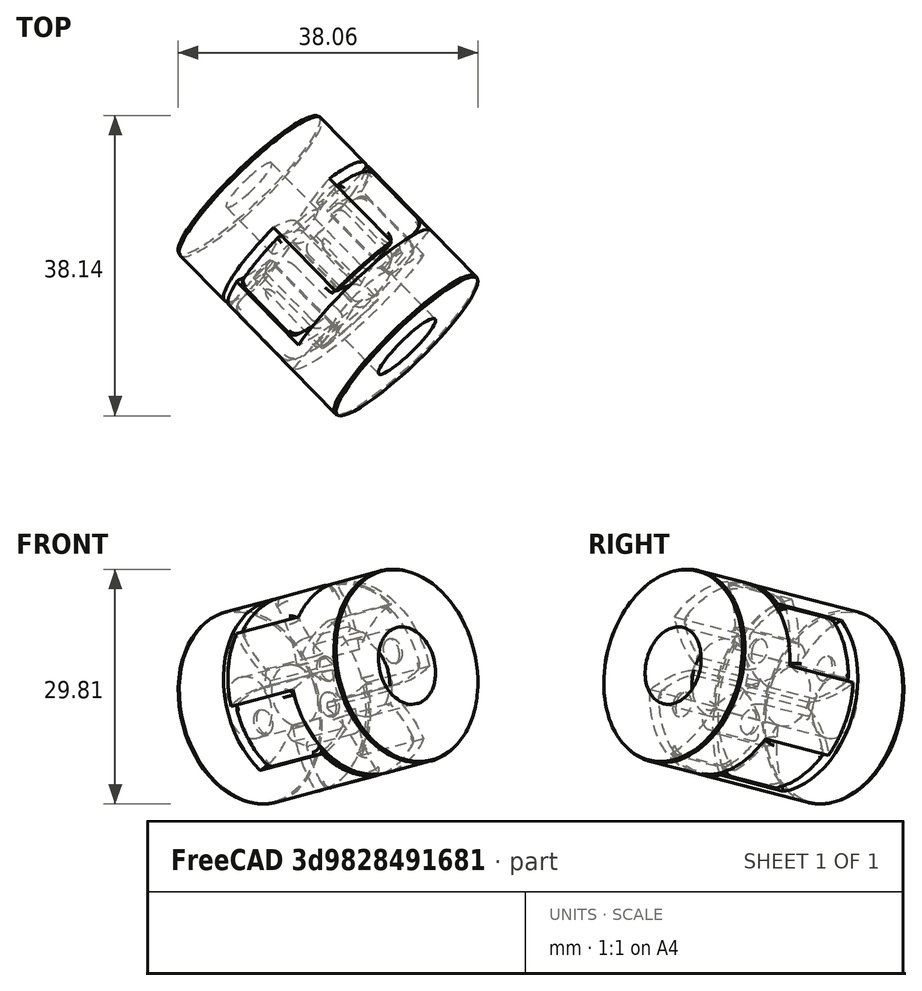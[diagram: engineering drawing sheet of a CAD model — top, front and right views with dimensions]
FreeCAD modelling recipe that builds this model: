
FCSTD DOCUMENT  (FreeCAD 0.21R38887 (Git))
Label: mufta8x10
License: All rights reserved
LicenseURL: http://en.wikipedia.org/wiki/All_rights_reserved
objects: Part::FeaturePython×5, Part::Feature×3, App::FeaturePython×2
note: 7 computed .brp shape members not serialized (recipe doc carries the construction recipe); baked Part::Feature solids carry a one-line shape summary decoded from their .brp

FEATURE [App::FeaturePython] Constraints  # WARN: FeaturePython — macro-defined, semantics opaque (R4)
  TreeRank = 9
  _LinkVersion = 1
  _Version = 1
FEATURE [Part::Feature] Solid  label="среднМуфта_8_10мм"
  InvalidShape = false
  Placement = pos=(-45.9665,58.8208,-32.3728) rot=(-0.885788,0.302008,-0.352379;2.03811rad)
  TreeRank = 1
  ValidateShape = false
  shape: bbox 24.52 x 25.47 x 27.67 mm, 100 faces (baked)
FEATURE [Part::Feature] Solid001  label="8мм^Муфта_8_10мм"
  InvalidShape = false
  Placement = pos=(-38.8086,51.5065,-30.4665) rot=(0.394242,0.904466,-0.162836;3.08092rad)
  TreeRank = 5
  ValidateShape = false
  shape: bbox 31.75 x 31.69 x 28.16 mm, 18 faces (baked)
FEATURE [Part::Feature] Solid002  label="10мм^Муфта_8_10мм"
  InvalidShape = false
  Placement = pos=(-46.2484,59.1089,-32.4479) rot=(0.798462,-0.457126,-0.391783;1.43227rad)
  TreeRank = 6
  ValidateShape = false
  shape: bbox 31.75 x 31.75 x 28.16 mm, 18 faces (baked)
FEATURE [Part::FeaturePython] Parts  # WARN: FeaturePython — macro-defined, semantics opaque (R4)
  Group = -> [Solid,Solid001,Solid002]
  GroupMode = 0
  InvalidShape = false
  TreeRank = 11
  ValidateShape = false
  _LinkVersion = 1
FEATURE [Part::FeaturePython] Assembly  label="Муфта_8_10мм001"  # WARN: FeaturePython — macro-defined, semantics opaque (R4)
  AutoRelax = true
  BuildShape = 0
  Freeze = false
  Group = -> [Constraints,Elements,Parts]
  InvalidShape = false
  TreeRank = 117
  ValidateShape = false
  Verbose = false
  _LinkVersion = 1
  _SolverType = 1
  _Version = 1
FEATURE [App::FeaturePython] Elements  # WARN: FeaturePython — macro-defined, semantics opaque (R4)
  Group = -> [Element,Element001,Element002]
  TreeRank = 10
  _LinkVersion = 1
FEATURE [Part::FeaturePython] Element  # link proxy (typed FeaturePython)
  Detach = false
  InvalidShape = false
  LinkTransform = true
  LinkedObject = -> Solid001 [Edge34]
  TreeRank = 118
  ValidateShape = false
  _LinkVersion = 1
  _Parent = -> Elements
FEATURE [Part::FeaturePython] Element001  # link proxy (typed FeaturePython)
  Detach = false
  InvalidShape = false
  LinkTransform = true
  LinkedObject = -> Solid002 [Edge16]
  TreeRank = 119
  ValidateShape = false
  _LinkVersion = 1
  _Parent = -> Elements
FEATURE [Part::FeaturePython] Element002  # link proxy (typed FeaturePython)
  Detach = false
  InvalidShape = false
  LinkTransform = true
  LinkedObject = -> Solid002 [Face7]
  TreeRank = 120
  ValidateShape = false
  _LinkVersion = 1
  _Parent = -> Elements
